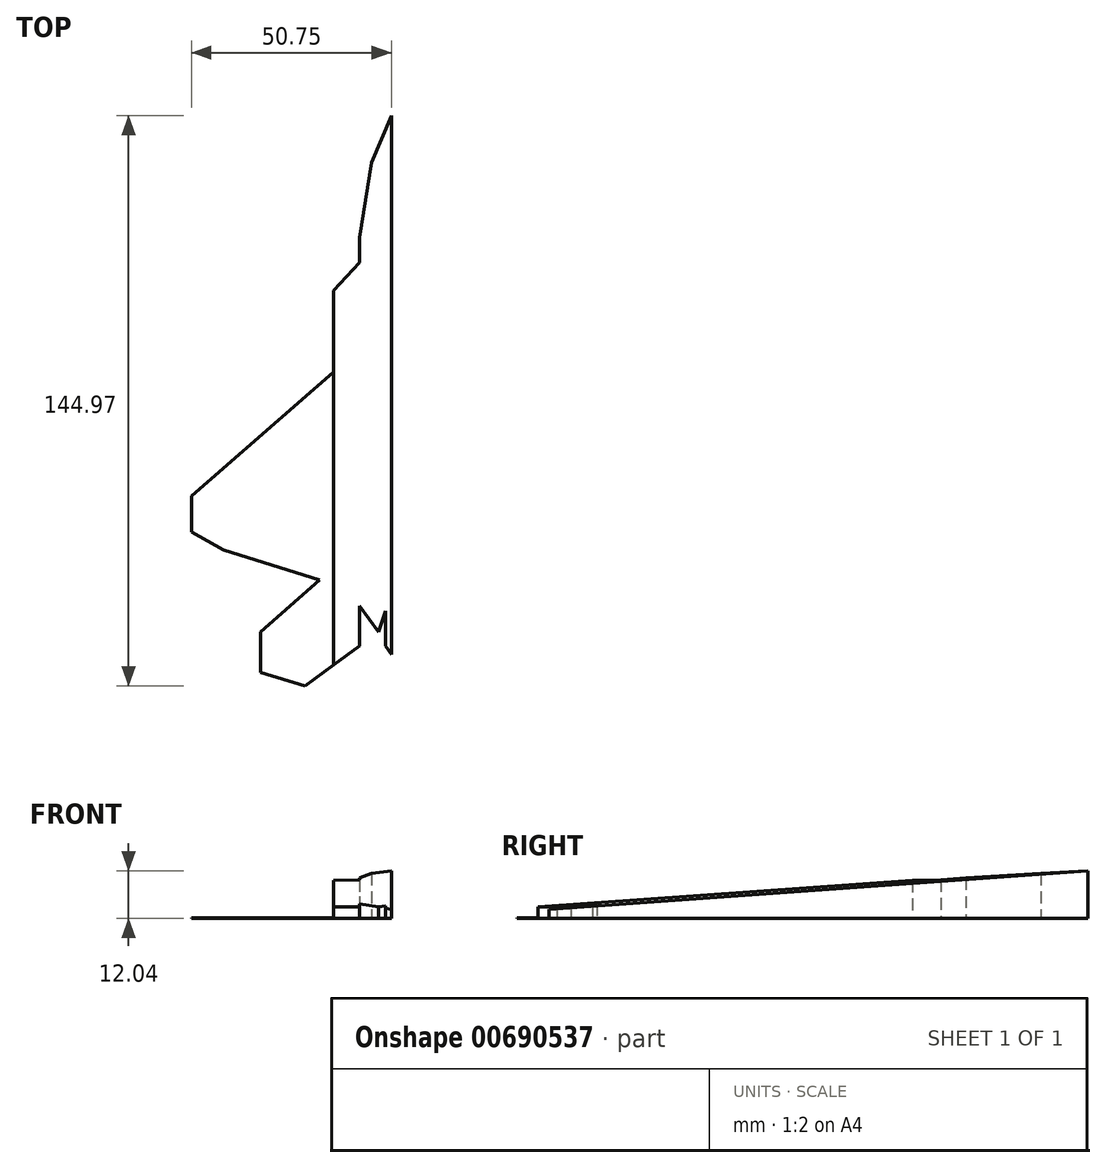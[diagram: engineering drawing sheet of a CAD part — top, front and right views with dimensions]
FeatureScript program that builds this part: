
annotation { "Feature Type Name" : "Feature", "Feature Type Description" : "" }
export const myFeature = defineFeature(function(context is Context, id is Id, definition is map)
    precondition{}
    {
        {
            var Q0;
            Q0=qCreatedBy(makeId("Top.planeOp"),FACE);
            var sketch = newSketch(context, id + "F0", { "sketchPlane" : qUnion([Q0])});
            skLineSegment(sketch, "E0", {"start": v(0, 71.49) * mm, "end": v(-4.96, 59.53) * mm, "construction": true});
            skLineSegment(sketch, "E1", {"start": v(-4.96, 59.53) * mm, "end": v(-8.01, 40.45) * mm, "construction": true});
            skLineSegment(sketch, "E2", {"start": v(-8.01, 40.45) * mm, "end": v(-8.01, 34.1) * mm, "construction": true});
            skLineSegment(sketch, "E3", {"start": v(-8.01, 34.1) * mm, "end": v(-14.63, 26.97) * mm, "construction": true});
            skLineSegment(sketch, "E4", {"start": v(-14.63, 26.97) * mm, "end": v(-14.63, 6.36) * mm, "construction": true});
            skLineSegment(sketch, "E5", {"start": v(-14.63, 6.36) * mm, "end": v(-50.75, -25.19) * mm});
            skLineSegment(sketch, "E6", {"start": v(-50.75, -25.19) * mm, "end": v(-50.75, -34.34) * mm});
            skLineSegment(sketch, "E7", {"start": v(-50.75, -34.34) * mm, "end": v(-42.61, -38.92) * mm});
            skLineSegment(sketch, "E8", {"start": v(-42.61, -38.92) * mm, "end": v(-18.19, -46.56) * mm});
            skLineSegment(sketch, "E9", {"start": v(-18.19, -46.56) * mm, "end": v(-33.2, -59.78) * mm});
            skLineSegment(sketch, "E10", {"start": v(-33.2, -59.78) * mm, "end": v(-33.2, -69.96) * mm});
            skLineSegment(sketch, "E11", {"start": v(-33.2, -69.96) * mm, "end": v(-21.93, -73.48) * mm});
            skLineSegment(sketch, "E12", {"start": v(-21.93, -73.48) * mm, "end": v(-8.01, -63.35) * mm});
            skLineSegment(sketch, "E13", {"start": v(-8.01, -63.35) * mm, "end": v(-8.01, -53.17) * mm, "construction": true});
            skPoint(sketch, "E13.endSnap0", {"position": v(-25.7, -53.17) * mm});
            skLineSegment(sketch, "E14", {"start": v(-8.01, -53.17) * mm, "end": v(-3.2, -59.78) * mm, "construction": true});
            skLineSegment(sketch, "E15", {"start": v(-3.2, -59.78) * mm, "end": v(-1.51, -54.4) * mm, "construction": true});
            skLineSegment(sketch, "E16", {"start": v(-1.51, -54.4) * mm, "end": v(-1.51, -63.35) * mm, "construction": true});
            skLineSegment(sketch, "E17", {"start": v(-1.51, -63.35) * mm, "end": v(0, -65.43) * mm, "construction": true});
            skLineSegment(sketch, "E18", {"start": v(0, -65.43) * mm, "end": v(0, 71.49) * mm, "construction": true});
            skLineSegment(sketch, "E19", {"start": v(0, 71.49) * mm, "end": v(-4.96, 59.53) * mm});
            skLineSegment(sketch, "E20", {"start": v(-8.01, 40.45) * mm, "end": v(-8.01, 34.1) * mm});
            skLineSegment(sketch, "E21", {"start": v(-14.63, 26.97) * mm, "end": v(-14.63, -68.16) * mm});
            skLineSegment(sketch, "E22", {"start": v(-14.63, -68.16) * mm, "end": v(-8.01, -63.35) * mm});
            skLineSegment(sketch, "E23", {"start": v(-8.01, -53.17) * mm, "end": v(-3.2, -59.78) * mm});
            skLineSegment(sketch, "E24", {"start": v(-1.51, -54.4) * mm, "end": v(-1.51, -63.35) * mm});
            skLineSegment(sketch, "E25", {"start": v(0, -65.43) * mm, "end": v(0, 71.49) * mm});
            skLineSegment(sketch, "E26", {"start": v(-14.63, 26.97) * mm, "end": v(-8.01, 34.1) * mm});
            skLineSegment(sketch, "E27", {"start": v(-8.01, 40.45) * mm, "end": v(-4.96, 59.53) * mm});
            skLineSegment(sketch, "E28", {"start": v(-8.01, -63.35) * mm, "end": v(-8.01, -53.17) * mm});
            skLineSegment(sketch, "E29", {"start": v(-3.2, -59.78) * mm, "end": v(-1.51, -54.4) * mm});
            skLineSegment(sketch, "E30", {"start": v(-1.51, -63.35) * mm, "end": v(0, -65.43) * mm});
            skSolve(sketch);
        }
        {
            var Q0;
            Q0 = qSketchRegion(id + "F0", true);
            extrude(context, id + "F1", {"entities" : qUnion([Q0]), "depth" : 0.1 * mm, "offsetDistance" : 25 * mm});
        }
        {
            var Q0;
            Q0=makeQuery(id+"F1.opExtrude","CAP_FACE",FACE,{"disambiguationData":[OSD([sQuery(id+"F0.wireOp",EDGE,"E5"),sQuery(id+"F0.wireOp",EDGE,"E6"),sQuery(id+"F0.wireOp",EDGE,"E7"),sQuery(id+"F0.wireOp",EDGE,"E8"),sQuery(id+"F0.wireOp",EDGE,"E9"),sQuery(id+"F0.wireOp",EDGE,"E10"),sQuery(id+"F0.wireOp",EDGE,"E11"),sQuery(id+"F0.wireOp",EDGE,"E12"),sQuery(id+"F0.wireOp",EDGE,"E19"),sQuery(id+"F0.wireOp",EDGE,"E20"),sQuery(id+"F0.wireOp",EDGE,"E21"),sQuery(id+"F0.wireOp",EDGE,"E22"),sQuery(id+"F0.wireOp",EDGE,"E23"),sQuery(id+"F0.wireOp",EDGE,"E24"),sQuery(id+"F0.wireOp",EDGE,"E25"),sQuery(id+"F0.wireOp",EDGE,"E26"),sQuery(id+"F0.wireOp",EDGE,"E27"),sQuery(id+"F0.wireOp",EDGE,"E28"),sQuery(id+"F0.wireOp",EDGE,"E29"),sQuery(id+"F0.wireOp",EDGE,"E30")])],"isStart":false});
            var sketch = newSketch(context, id + "F2", { "sketchPlane" : qUnion([Q0])});
            skLineSegment(sketch, "E31", {"start": v(0, 71.49) * mm, "end": v(-4.96, 59.53) * mm});
            skLineSegment(sketch, "E32", {"start": v(-4.96, 59.53) * mm, "end": v(-8.01, 40.45) * mm});
            skLineSegment(sketch, "E33", {"start": v(-8.01, 40.45) * mm, "end": v(-8.01, 34.1) * mm});
            skLineSegment(sketch, "E34", {"start": v(-8.01, 34.1) * mm, "end": v(-14.63, 26.97) * mm});
            skLineSegment(sketch, "E35", {"start": v(-14.63, 26.97) * mm, "end": v(-14.63, -68.16) * mm});
            skLineSegment(sketch, "E36", {"start": v(-14.63, -68.16) * mm, "end": v(-8.01, -63.35) * mm});
            skLineSegment(sketch, "E37", {"start": v(-8.01, -63.35) * mm, "end": v(-8.01, -53.17) * mm});
            skLineSegment(sketch, "E38", {"start": v(-8.01, -53.17) * mm, "end": v(-3.2, -59.78) * mm});
            skLineSegment(sketch, "E39", {"start": v(-3.2, -59.78) * mm, "end": v(-1.51, -54.4) * mm});
            skLineSegment(sketch, "E40", {"start": v(-1.51, -54.4) * mm, "end": v(-1.51, -63.35) * mm});
            skLineSegment(sketch, "E41", {"start": v(-1.51, -63.35) * mm, "end": v(0, -65.43) * mm});
            skLineSegment(sketch, "E42", {"start": v(0, -65.43) * mm, "end": v(0, 71.49) * mm});
            skSolve(sketch);
        }
        {
            var Q0;
            Q0 = qSketchRegion(id + "F2", true);
            extrude(context, id + "F3", {"entities" : qUnion([Q0]), "operationType" : NewBodyOperationType.ADD, "depth" : 12 * mm, "offsetDistance" : 25 * mm});
        }
        {
            var Q0;
            Q0=makeQuery(id+"F3.opExtrude","CAP_EDGE",EDGE,{"disambiguationData":[OSD([sQuery(id+"F2.wireOp",EDGE,"E36")])],"isStart":false});
            chamfer(context, id + "F4", {"entities" : qUnion([Q0]), "chamferType" : ChamferType.OFFSET_ANGLE, "width" : 105 * mm, "oppositeDirection" : false, "angle" : 5 * degree, "tangentPropagation" : true});
        }
    });
